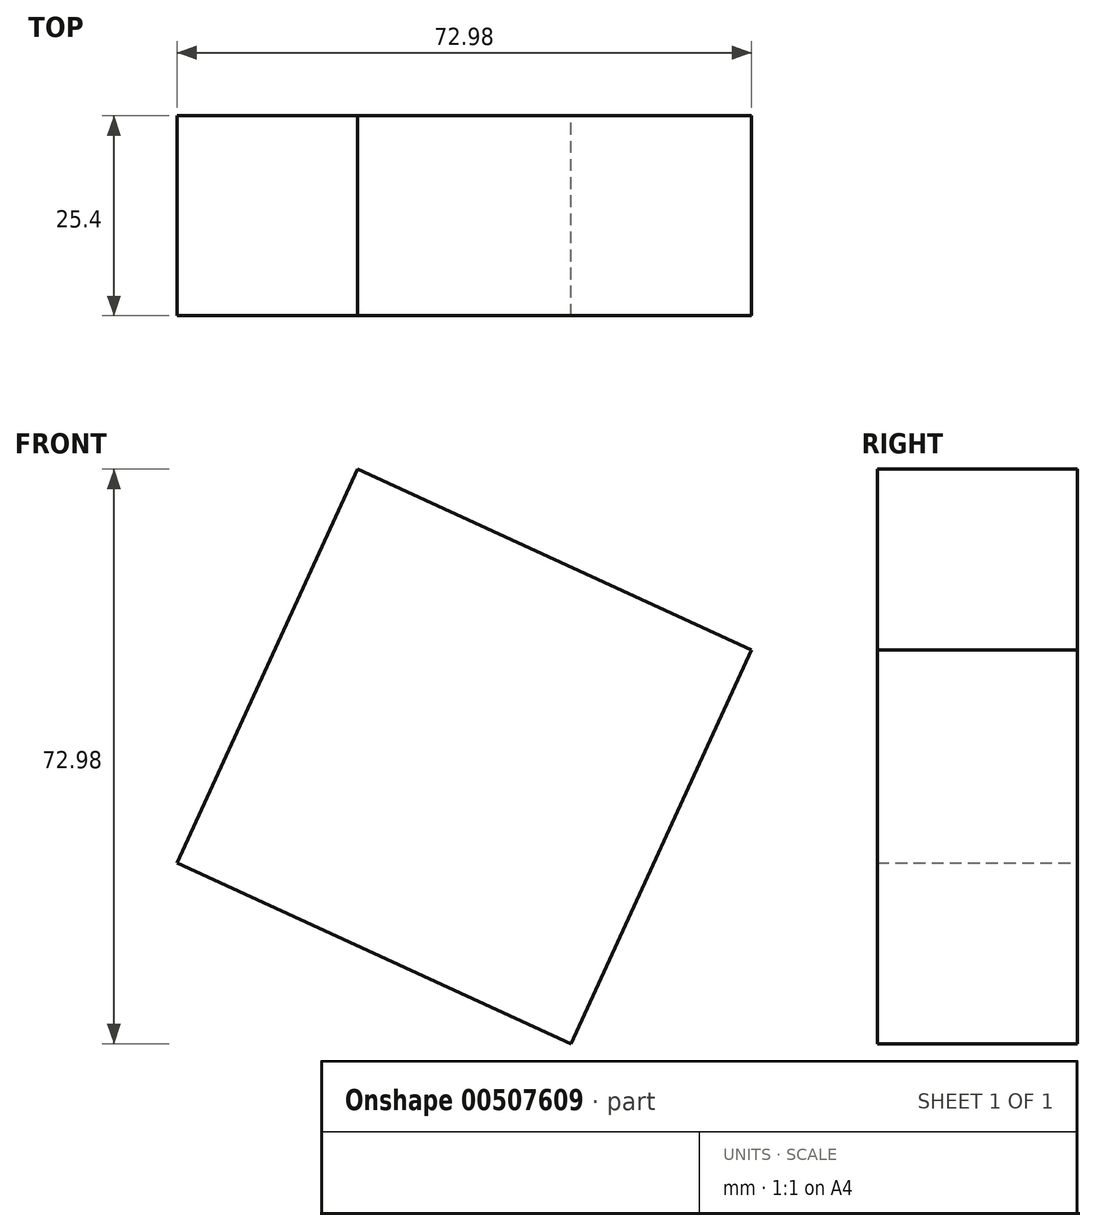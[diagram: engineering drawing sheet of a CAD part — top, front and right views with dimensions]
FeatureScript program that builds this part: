
annotation { "Feature Type Name" : "Feature", "Feature Type Description" : "" }
export const myFeature = defineFeature(function(context is Context, id is Id, definition is map)
    precondition{}
    {
        {
            var Q0;
            Q0=qCreatedBy(makeId("Front.planeOp"),FACE);
            var sketch = newSketch(context, id + "F0", { "sketchPlane" : qUnion([Q0])});
            skCircle(sketch, "E0.cCircle", {"center": v(0, 0) * mm, "radius": 38.93 * mm, "construction": true});
            skLineSegment(sketch, "E0.0", {"start": v(-13.56, 36.5) * mm, "end": v(36.5, 13.56) * mm});
            skLineSegment(sketch, "E0.1", {"start": v(36.5, 13.56) * mm, "end": v(13.56, -36.5) * mm});
            skLineSegment(sketch, "E0.2", {"start": v(13.56, -36.5) * mm, "end": v(-36.5, -13.56) * mm});
            skLineSegment(sketch, "E0.3", {"start": v(-36.5, -13.56) * mm, "end": v(-13.56, 36.5) * mm});
            skSolve(sketch);
        }
        {
            var Q0;
            Q0 = qSketchRegion(id + "F0", true);
            extrude(context, id + "F1", {"entities" : qUnion([Q0]), "depth" : 25.4 * mm});
        }
    });
